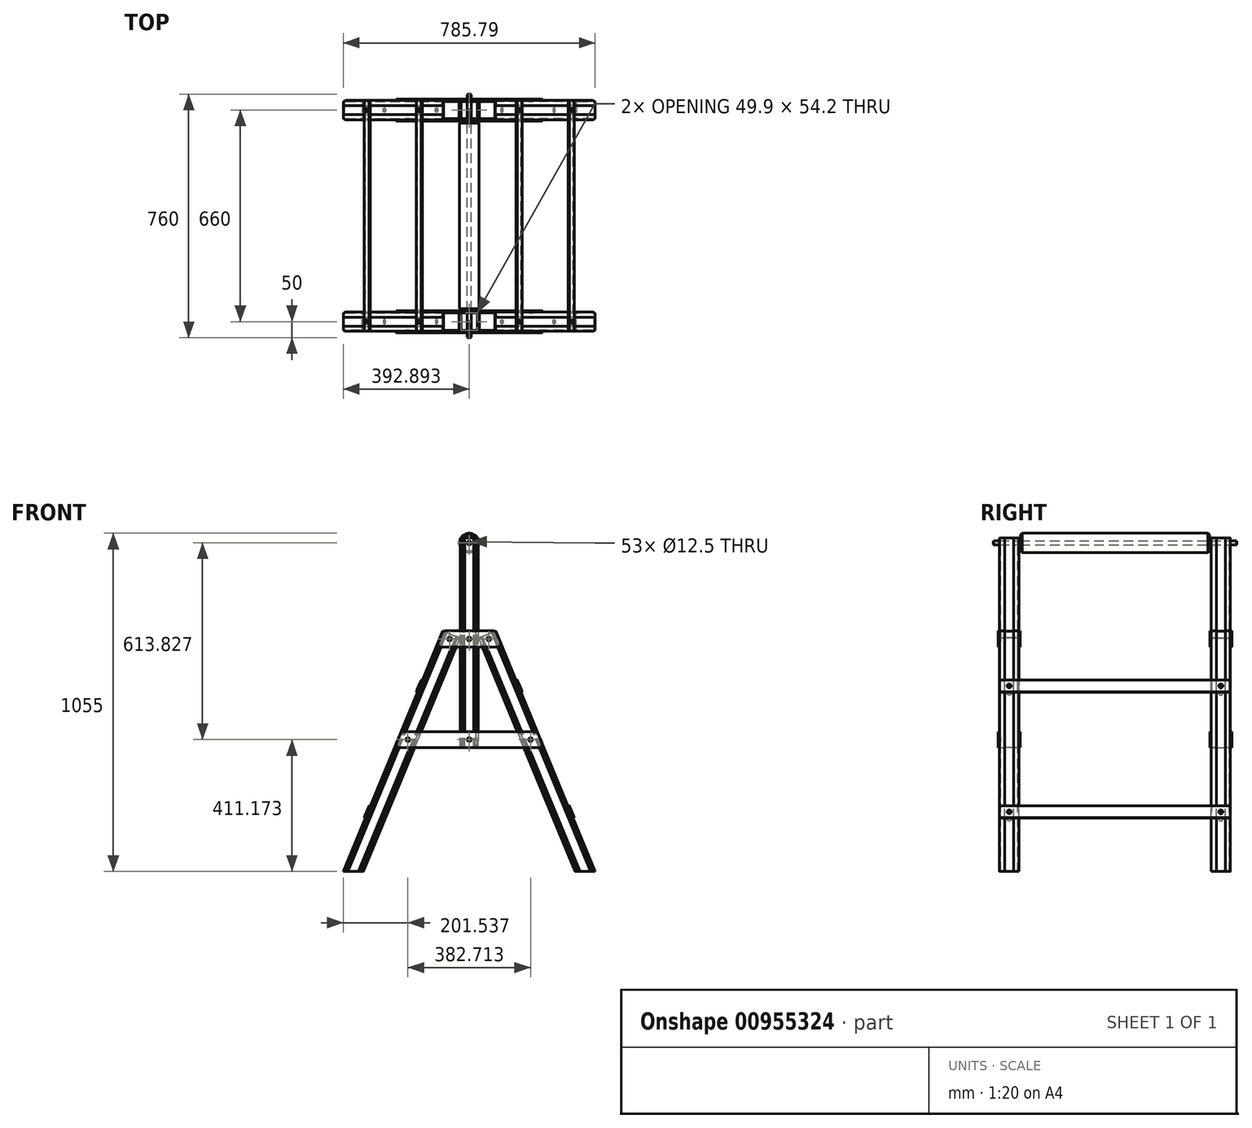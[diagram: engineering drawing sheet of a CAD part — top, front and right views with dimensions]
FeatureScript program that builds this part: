
annotation { "Feature Type Name" : "Feature", "Feature Type Description" : "" }
export const myFeature = defineFeature(function(context is Context, id is Id, definition is map)
    precondition{}
    {
        {
            var Q0;
            Q0=qCreatedBy(makeId("Front.planeOp"),FACE);
            var sketch = newSketch(context, id + "F0", { "sketchPlane" : qUnion([Q0])});
            skLineSegment(sketch, "E0", {"start": v(0, 0) * mm, "end": v(-310.74, 750.2) * mm});
            skLineSegment(sketch, "E1", {"start": v(-310.74, 750.2) * mm, "end": v(-364.05, 728.1) * mm});
            skLineSegment(sketch, "E2", {"start": v(-364.05, 728.1) * mm, "end": v(-62.45, 0) * mm});
            skLineSegment(sketch, "E3", {"start": v(-62.45, 0) * mm, "end": v(0, 0) * mm});
            skLineSegment(sketch, "E4", {"start": v(-337.4, 739.15) * mm, "end": v(-31.23, 0) * mm, "construction": true});
            skCircle(sketch, "E5", {"center": v(-331.65, 725.3) * mm, "radius": 6.25 * mm});
            skCircle(sketch, "E6", {"center": v(-201.54, 411.17) * mm, "radius": 6.25 * mm});
            skSolve(sketch);
        }
        {
            var Q0;
            Q0=qSketchRegion(id+"F0",true);
            extrude(context, id + "F1", {"entities" : qUnion([Q0]), "depth" : 60 * mm, "offsetDistance" : 25 * mm});
        }
        {
            var Q0;
            Q0=makeQuery(id+"F1.opExtrude","CAP_EDGE",EDGE,{"disambiguationData":[OSD([sQuery(id+"F0.wireOp",EDGE,"E0")])],"isStart":false});
            var Q1;
            Q1=makeQuery(id+"F1.opExtrude","CAP_EDGE",EDGE,{"disambiguationData":[OSD([sQuery(id+"F0.wireOp",EDGE,"E2")])],"isStart":false});
            var Q2;
            Q2=makeQuery(id+"F1.opExtrude","CAP_EDGE",EDGE,{"disambiguationData":[OSD([sQuery(id+"F0.wireOp",EDGE,"E0")])],"isStart":true});
            var Q3;
            Q3=makeQuery(id+"F1.opExtrude","CAP_EDGE",EDGE,{"disambiguationData":[OSD([sQuery(id+"F0.wireOp",EDGE,"E2")])],"isStart":true});
            fillet(context, id + "F2", {"entities" : qUnion([Q0, Q1, Q2, Q3]), "radius" : 7.5 * mm, "tangentPropagation" : true, "allowEdgeOverflow" : false});
        }
        {
            var Q0;
            Q0=makeQuery(id+"F1.opExtrude","SWEPT_FACE",FACE,{"disambiguationData":[OSD([sQuery(id+"F0.wireOp",EDGE,"E1")])]});
            var sketch = newSketch(context, id + "F3", { "sketchPlane" : qUnion([Q0])});
            skLineSegment(sketch, "E7", {"start": v(-50.2, -60) * mm, "end": v(-49.2, -59) * mm});
            skLineSegment(sketch, "E8", {"start": v(-49.2, -59) * mm, "end": v(-48.2, -60) * mm});
            skLineSegment(sketch, "E9", {"start": v(-48.2, -60) * mm, "end": v(-47.2, -59) * mm});
            skLineSegment(sketch, "E10", {"start": v(-47.2, -59) * mm, "end": v(-46.2, -60) * mm});
            skLineSegment(sketch, "E11", {"start": v(-46.2, -60) * mm, "end": v(-45.2, -59) * mm});
            skLineSegment(sketch, "E12", {"start": v(-45.2, -59) * mm, "end": v(-44.2, -60) * mm});
            skLineSegment(sketch, "E13", {"start": v(-28.85, -60) * mm, "end": v(-28.85, -30) * mm, "construction": true});
            skPoint(sketch, "E13.endSnap0", {"position": v(-57.7, -30) * mm});
            skLineSegment(sketch, "E14", {"start": v(-28.85, -30) * mm, "end": v(-57.7, -30) * mm, "construction": true});
            skLineSegment(sketch, "E15", {"start": v(-57.4, -44) * mm, "end": v(-57.7, -44) * mm});
            skLineSegment(sketch, "E16", {"start": v(-57.4, -44) * mm, "end": v(-57.4, -30) * mm});
            skArc(sketch, "E17.0", {"start": v(-54.8, -52.5) * mm, "mid": v(-53.45, -55.75) * mm, "end": v(-50.2, -57.1) * mm});
            skLineSegment(sketch, "E18", {"start": v(-54.8, -52.5) * mm, "end": v(-54.8, -30) * mm});
            skLineSegment(sketch, "E19", {"start": v(-50.2, -57.1) * mm, "end": v(-28.85, -57.1) * mm});
            skLineSegment(sketch, "E20.MirrorCS", {"start": v(-0.3, -44) * mm, "end": v(0, -44) * mm});
            skLineSegment(sketch, "E21.MirrorCS", {"start": v(-7.5, -60) * mm, "end": v(-8.5, -59) * mm});
            skLineSegment(sketch, "E22.MirrorCS", {"start": v(-11.5, -60) * mm, "end": v(-12.5, -59) * mm});
            skLineSegment(sketch, "E23.MirrorCS", {"start": v(-9.5, -60) * mm, "end": v(-10.5, -59) * mm});
            skLineSegment(sketch, "E24.MirrorCS", {"start": v(-12.5, -59) * mm, "end": v(-13.5, -60) * mm});
            skLineSegment(sketch, "E25.MirrorCS", {"start": v(-10.5, -59) * mm, "end": v(-11.5, -60) * mm});
            skLineSegment(sketch, "E26.MirrorCS", {"start": v(-8.5, -59) * mm, "end": v(-9.5, -60) * mm});
            skArc(sketch, "E27.MirrorCS", {"start": v(-2.9, -52.5) * mm, "mid": v(-4.25, -55.75) * mm, "end": v(-7.5, -57.1) * mm});
            skLineSegment(sketch, "E28.MirrorCS", {"start": v(-0.3, -44) * mm, "end": v(-0.3, -30) * mm});
            skLineSegment(sketch, "E29.MirrorCS", {"start": v(-7.5, -57.1) * mm, "end": v(-28.85, -57.1) * mm});
            skLineSegment(sketch, "E30.MirrorCS", {"start": v(-2.9, -52.5) * mm, "end": v(-2.9, -30) * mm});
            skLineSegment(sketch, "E31.MirrorCS", {"start": v(-50.2, 0) * mm, "end": v(-49.2, -1) * mm});
            skLineSegment(sketch, "E32.MirrorCS", {"start": v(-48.2, 0) * mm, "end": v(-47.2, -1) * mm});
            skLineSegment(sketch, "E33.MirrorCS", {"start": v(-49.2, -1) * mm, "end": v(-48.2, 0) * mm});
            skLineSegment(sketch, "E34.MirrorCS", {"start": v(-46.2, 0) * mm, "end": v(-45.2, -1) * mm});
            skLineSegment(sketch, "E35.MirrorCS", {"start": v(-47.2, -1) * mm, "end": v(-46.2, 0) * mm});
            skLineSegment(sketch, "E36.MirrorCS", {"start": v(-57.4, -16) * mm, "end": v(-57.7, -16) * mm});
            skLineSegment(sketch, "E37.MirrorCS", {"start": v(-45.2, -1) * mm, "end": v(-44.2, 0) * mm});
            skArc(sketch, "E38.MirrorCS", {"start": v(-54.8, -7.5) * mm, "mid": v(-53.45, -4.25) * mm, "end": v(-50.2, -2.9) * mm});
            skLineSegment(sketch, "E39.MirrorCS", {"start": v(-50.2, -2.9) * mm, "end": v(-28.85, -2.9) * mm});
            skLineSegment(sketch, "E40.MirrorCS", {"start": v(-54.8, -7.5) * mm, "end": v(-54.8, -30) * mm});
            skLineSegment(sketch, "E41.MirrorCS", {"start": v(-57.4, -16) * mm, "end": v(-57.4, -30) * mm});
            skLineSegment(sketch, "E42.MirrorCS", {"start": v(-9.5, 0) * mm, "end": v(-10.5, -1) * mm});
            skLineSegment(sketch, "E43.MirrorCS", {"start": v(-12.5, -1) * mm, "end": v(-13.5, 0) * mm});
            skLineSegment(sketch, "E44.MirrorCS", {"start": v(-10.5, -1) * mm, "end": v(-11.5, 0) * mm});
            skLineSegment(sketch, "E45.MirrorCS", {"start": v(-0.3, -16) * mm, "end": v(0, -16) * mm});
            skLineSegment(sketch, "E46.MirrorCS", {"start": v(-11.5, 0) * mm, "end": v(-12.5, -1) * mm});
            skLineSegment(sketch, "E47.MirrorCS", {"start": v(-7.5, 0) * mm, "end": v(-8.5, -1) * mm});
            skLineSegment(sketch, "E48.MirrorCS", {"start": v(-8.5, -1) * mm, "end": v(-9.5, 0) * mm});
            skLineSegment(sketch, "E49.MirrorCS", {"start": v(-2.9, -7.5) * mm, "end": v(-2.9, -30) * mm});
            skLineSegment(sketch, "E50.MirrorCS", {"start": v(-7.5, -2.9) * mm, "end": v(-28.85, -2.9) * mm});
            skArc(sketch, "E51.MirrorCS", {"start": v(-2.9, -7.5) * mm, "mid": v(-4.25, -4.25) * mm, "end": v(-7.5, -2.9) * mm});
            skLineSegment(sketch, "E52.MirrorCS", {"start": v(-0.3, -16) * mm, "end": v(-0.3, -30) * mm});
            skSolve(sketch);
        }
        {
            var Q0;
            Q0=makeQuery(id+"F3.imprint","IMPRINT",FACE,{"disambiguationData":[TD([[makeQuery(id+"F3.imprint","IMPRINT",EDGE,{"derivedFrom":sQuery(id+"F3.wireOp",EDGE,"E17.0")}),1.0]])]});
            var Q1;
            {var subQ0=sQuery(id+"F3.wireOp",EDGE,"E34.MirrorCS");Q1=makeQuery(id+"F3.imprint","IMPRINT",FACE,{"disambiguationData":[TD([[makeQuery(id+"F3.imprint","IMPRINT",EDGE,{"derivedFrom":subQ0}),1.0]])]});}
            var Q2;
            {var subQ0=sQuery(id+"F3.wireOp",EDGE,"E32.MirrorCS");Q2=makeQuery(id+"F3.imprint","IMPRINT",FACE,{"disambiguationData":[TD([[makeQuery(id+"F3.imprint","IMPRINT",EDGE,{"derivedFrom":subQ0}),1.0]])]});}
            var Q3;
            {var subQ0=sQuery(id+"F3.wireOp",EDGE,"E31.MirrorCS");Q3=makeQuery(id+"F3.imprint","IMPRINT",FACE,{"disambiguationData":[TD([[makeQuery(id+"F3.imprint","IMPRINT",EDGE,{"derivedFrom":subQ0}),1.0]])]});}
            var Q4;
            {var subQ1=sQuery(id+"F3.wireOp",EDGE,"E15");Q4=makeQuery(id+"F3.imprint","IMPRINT",FACE,{"disambiguationData":[TD([[makeQuery(id+"F3.imprint","IMPRINT",EDGE,{"derivedFrom":subQ1}),-1.0]])]});}
            var Q5;
            {var subQ0=sQuery(id+"F3.wireOp",EDGE,"E7");Q5=makeQuery(id+"F3.imprint","IMPRINT",FACE,{"disambiguationData":[TD([[makeQuery(id+"F3.imprint","IMPRINT",EDGE,{"derivedFrom":subQ0}),-1.0]])]});}
            var Q6;
            {var subQ0=sQuery(id+"F3.wireOp",EDGE,"E9");Q6=makeQuery(id+"F3.imprint","IMPRINT",FACE,{"disambiguationData":[TD([[makeQuery(id+"F3.imprint","IMPRINT",EDGE,{"derivedFrom":subQ0}),-1.0]])]});}
            var Q7;
            {var subQ0=sQuery(id+"F3.wireOp",EDGE,"E11");Q7=makeQuery(id+"F3.imprint","IMPRINT",FACE,{"disambiguationData":[TD([[makeQuery(id+"F3.imprint","IMPRINT",EDGE,{"derivedFrom":subQ0}),-1.0]])]});}
            var Q8;
            {var subQ0=sQuery(id+"F3.wireOp",EDGE,"E21.MirrorCS");Q8=makeQuery(id+"F3.imprint","IMPRINT",FACE,{"disambiguationData":[TD([[makeQuery(id+"F3.imprint","IMPRINT",EDGE,{"derivedFrom":subQ0}),1.0]])]});}
            var Q9;
            {var subQ0=sQuery(id+"F3.wireOp",EDGE,"E23.MirrorCS");Q9=makeQuery(id+"F3.imprint","IMPRINT",FACE,{"disambiguationData":[TD([[makeQuery(id+"F3.imprint","IMPRINT",EDGE,{"derivedFrom":subQ0}),1.0]])]});}
            var Q10;
            {var subQ0=sQuery(id+"F3.wireOp",EDGE,"E22.MirrorCS");Q10=makeQuery(id+"F3.imprint","IMPRINT",FACE,{"disambiguationData":[TD([[makeQuery(id+"F3.imprint","IMPRINT",EDGE,{"derivedFrom":subQ0}),1.0]])]});}
            var Q11;
            {var subQ1=sQuery(id+"F3.wireOp",EDGE,"E20.MirrorCS");Q11=makeQuery(id+"F3.imprint","IMPRINT",FACE,{"disambiguationData":[TD([[makeQuery(id+"F3.imprint","IMPRINT",EDGE,{"derivedFrom":subQ1}),1.0]])]});}
            var Q12;
            {var subQ0=sQuery(id+"F3.wireOp",EDGE,"E47.MirrorCS");Q12=makeQuery(id+"F3.imprint","IMPRINT",FACE,{"disambiguationData":[TD([[makeQuery(id+"F3.imprint","IMPRINT",EDGE,{"derivedFrom":subQ0}),-1.0]])]});}
            var Q13;
            {var subQ0=sQuery(id+"F3.wireOp",EDGE,"E42.MirrorCS");Q13=makeQuery(id+"F3.imprint","IMPRINT",FACE,{"disambiguationData":[TD([[makeQuery(id+"F3.imprint","IMPRINT",EDGE,{"derivedFrom":subQ0}),-1.0]])]});}
            var Q14;
            {var subQ0=sQuery(id+"F3.wireOp",EDGE,"E43.MirrorCS");Q14=makeQuery(id+"F3.imprint","IMPRINT",FACE,{"disambiguationData":[TD([[makeQuery(id+"F3.imprint","IMPRINT",EDGE,{"derivedFrom":subQ0}),-1.0]])]});}
            var Q15;
            Q15=makeQuery(id+"F1.opExtrude","SWEPT_FACE",FACE,{"disambiguationData":[OSD([sQuery(id+"F0.wireOp",EDGE,"E3")])]});
            extrude(context, id + "F4", {"entities" : qUnion([Q0, Q1, Q2, Q3, Q4, Q5, Q6, Q7, Q8, Q9, Q10, Q11, Q12, Q13, Q14]), "operationType" : NewBodyOperationType.REMOVE, "endBound" : BoundingType.UP_TO_SURFACE, "oppositeDirection" : true, "depth" : 25 * mm, "endBoundEntityFace" : qUnion([Q15]), "offsetDistance" : 25 * mm});
        }
        {
            var Q0;
            {var subQ0=sQuery(id+"F0.wireOp",EDGE,"E0");Q0=makeQuery(id+"F4.boolean.opBoolean","SPLIT",FACE,{"disambiguationData":[TD([makeQuery(id+"F4.opExtrude","SWEPT_FACE",FACE,{"disambiguationData":[OSD([sQuery(id+"F3.wireOp",EDGE,"E20.MirrorCS")])]})])],"derivedFrom":makeQuery(id+"F1.opExtrude","SWEPT_FACE",FACE,{"disambiguationData":[OSD([subQ0])]})});}
            var sketch = newSketch(context, id + "F5", { "sketchPlane" : qUnion([Q0])});
            skLineSegment(sketch, "E53", {"start": v(-60, 0) * mm, "end": v(0, 0) * mm, "construction": true});
            skLineSegment(sketch, "E54", {"start": v(-30, 0) * mm, "end": v(-30, 812) * mm, "construction": true});
            skCircle(sketch, "E55", {"center": v(-30, 200) * mm, "radius": 6.25 * mm});
            skCircle(sketch, "E56", {"center": v(-30, 625) * mm, "radius": 6.25 * mm});
            skSolve(sketch);
        }
        {
            var Q0;
            Q0=qSketchRegion(id+"F5",true);
            var Q1;
            {var subQ0=sQuery(id+"F0.wireOp",EDGE,"E2");Q1=makeQuery(id+"F4.boolean.opBoolean","SPLIT",FACE,{"disambiguationData":[TD([makeQuery(id+"F4.opExtrude","SWEPT_FACE",FACE,{"disambiguationData":[OSD([sQuery(id+"F3.wireOp",EDGE,"E15")])]})])],"derivedFrom":makeQuery(id+"F1.opExtrude","SWEPT_FACE",FACE,{"disambiguationData":[OSD([subQ0])]})});}
            extrude(context, id + "F6", {"entities" : qUnion([Q0]), "operationType" : NewBodyOperationType.REMOVE, "endBound" : BoundingType.UP_TO_SURFACE, "oppositeDirection" : true, "depth" : 25 * mm, "endBoundEntityFace" : qUnion([Q1]), "offsetDistance" : 25 * mm});
        }
        {
            var Q0;
            Q0=makeQuery(id+"F1.opExtrude","CAP_FACE",FACE,{"disambiguationData":[OSD([sQuery(id+"F0.wireOp",EDGE,"E0"),sQuery(id+"F0.wireOp",EDGE,"E1"),sQuery(id+"F0.wireOp",EDGE,"E2"),sQuery(id+"F0.wireOp",EDGE,"E3")])],"isStart":false});
            var sketch = newSketch(context, id + "F7", { "sketchPlane" : qUnion([Q0])});
            skLineSegment(sketch, "E57", {"start": v(-365.05, 1040) * mm, "end": v(-365.05, 386.17) * mm});
            skLineSegment(sketch, "E58", {"start": v(-365.05, 386.17) * mm, "end": v(-420.75, 386.17) * mm});
            skLineSegment(sketch, "E59", {"start": v(-420.75, 386.17) * mm, "end": v(-420.75, 1040) * mm});
            skLineSegment(sketch, "E60", {"start": v(-420.75, 1040) * mm, "end": v(-365.05, 1040) * mm});
            skLineSegment(sketch, "E61", {"start": v(-392.9, 386.17) * mm, "end": v(-392.9, 1040) * mm, "construction": true});
            skCircle(sketch, "E62", {"center": v(-392.9, 725.3) * mm, "radius": 6.25 * mm});
            skLineSegment(sketch, "E63", {"start": v(-420.75, 719.04) * mm, "end": v(-297.84, 719.04) * mm, "construction": true});
            skLineSegment(sketch, "E64", {"start": v(-420.75, 404.92) * mm, "end": v(-167.72, 404.92) * mm, "construction": true});
            skCircle(sketch, "E65", {"center": v(-392.9, 411.17) * mm, "radius": 6.25 * mm});
            skCircle(sketch, "E66", {"center": v(-392.9, 1025) * mm, "radius": 6.25 * mm});
            skSolve(sketch);
        }
        {
            var Q0;
            Q0=qSketchRegion(id+"F7",true);
            extrude(context, id + "F8", {"entities" : qUnion([Q0]), "oppositeDirection" : true, "depth" : 60 * mm, "offsetDistance" : 25 * mm});
        }
        {
            var Q0;
            Q0=makeQuery(id+"F8.opExtrude","CAP_EDGE",EDGE,{"disambiguationData":[OSD([sQuery(id+"F7.wireOp",EDGE,"E59")])],"isStart":true});
            var Q1;
            Q1=makeQuery(id+"F8.opExtrude","CAP_EDGE",EDGE,{"disambiguationData":[OSD([sQuery(id+"F7.wireOp",EDGE,"E57")])],"isStart":true});
            var Q2;
            Q2=makeQuery(id+"F8.opExtrude","CAP_EDGE",EDGE,{"disambiguationData":[OSD([sQuery(id+"F7.wireOp",EDGE,"E57")])],"isStart":false});
            var Q3;
            Q3=makeQuery(id+"F8.opExtrude","CAP_EDGE",EDGE,{"disambiguationData":[OSD([sQuery(id+"F7.wireOp",EDGE,"E59")])],"isStart":false});
            fillet(context, id + "F9", {"entities" : qUnion([Q0, Q1, Q2, Q3]), "radius" : 7.5 * mm, "tangentPropagation" : true, "allowEdgeOverflow" : false});
        }
        {
            var Q0;
            Q0=makeQuery(id+"F8.opExtrude","SWEPT_FACE",FACE,{"disambiguationData":[OSD([sQuery(id+"F7.wireOp",EDGE,"E60")])]});
            var sketch = newSketch(context, id + "F10", { "sketchPlane" : qUnion([Q0])});
            skLineSegment(sketch, "E67", {"start": v(-420.75, -30) * mm, "end": v(-392.9, -30) * mm, "construction": true});
            skPoint(sketch, "E67.endSnap0", {"position": v(-392.9, -60) * mm});
            skLineSegment(sketch, "E68", {"start": v(-392.9, -30) * mm, "end": v(-392.9, -60) * mm, "construction": true});
            skLineSegment(sketch, "E69", {"start": v(-413.25, -60) * mm, "end": v(-412.25, -59) * mm});
            skLineSegment(sketch, "E70", {"start": v(-412.25, -59) * mm, "end": v(-411.25, -60) * mm});
            skLineSegment(sketch, "E71", {"start": v(-420.45, -30) * mm, "end": v(-420.45, -44) * mm});
            skLineSegment(sketch, "E72", {"start": v(-420.45, -44) * mm, "end": v(-420.75, -44) * mm});
            skLineSegment(sketch, "E73", {"start": v(-411.25, -60) * mm, "end": v(-410.25, -59) * mm});
            skLineSegment(sketch, "E74", {"start": v(-410.25, -59) * mm, "end": v(-409.25, -60) * mm});
            skLineSegment(sketch, "E75", {"start": v(-409.25, -60) * mm, "end": v(-408.25, -59) * mm});
            skLineSegment(sketch, "E76", {"start": v(-408.25, -59) * mm, "end": v(-407.25, -60) * mm});
            skArc(sketch, "E77.0", {"start": v(-417.85, -52.5) * mm, "mid": v(-416.5, -55.75) * mm, "end": v(-413.25, -57.1) * mm});
            skLineSegment(sketch, "E78", {"start": v(-417.85, -52.5) * mm, "end": v(-417.85, -30) * mm});
            skLineSegment(sketch, "E79", {"start": v(-413.25, -57.1) * mm, "end": v(-392.9, -57.1) * mm});
            skLineSegment(sketch, "E80.MirrorCS", {"start": v(-365.35, -44) * mm, "end": v(-365.05, -44) * mm});
            skLineSegment(sketch, "E81.MirrorCS", {"start": v(-372.55, -60) * mm, "end": v(-373.55, -59) * mm});
            skLineSegment(sketch, "E82.MirrorCS", {"start": v(-373.55, -59) * mm, "end": v(-374.55, -60) * mm});
            skLineSegment(sketch, "E83.MirrorCS", {"start": v(-377.55, -59) * mm, "end": v(-378.55, -60) * mm});
            skLineSegment(sketch, "E84.MirrorCS", {"start": v(-374.55, -60) * mm, "end": v(-375.55, -59) * mm});
            skLineSegment(sketch, "E85.MirrorCS", {"start": v(-375.55, -59) * mm, "end": v(-376.55, -60) * mm});
            skLineSegment(sketch, "E86.MirrorCS", {"start": v(-376.55, -60) * mm, "end": v(-377.55, -59) * mm});
            skArc(sketch, "E87.MirrorCS", {"start": v(-367.95, -52.5) * mm, "mid": v(-369.3, -55.75) * mm, "end": v(-372.55, -57.1) * mm});
            skLineSegment(sketch, "E88.MirrorCS", {"start": v(-365.35, -30) * mm, "end": v(-365.35, -44) * mm});
            skLineSegment(sketch, "E89.MirrorCS", {"start": v(-372.55, -57.1) * mm, "end": v(-392.9, -57.1) * mm});
            skLineSegment(sketch, "E90.MirrorCS", {"start": v(-367.95, -52.5) * mm, "end": v(-367.95, -30) * mm});
            skLineSegment(sketch, "E91.MirrorCS", {"start": v(-411.25, 0) * mm, "end": v(-410.25, -1) * mm});
            skLineSegment(sketch, "E92.MirrorCS", {"start": v(-413.25, 0) * mm, "end": v(-412.25, -1) * mm});
            skLineSegment(sketch, "E93.MirrorCS", {"start": v(-412.25, -1) * mm, "end": v(-411.25, 0) * mm});
            skLineSegment(sketch, "E94.MirrorCS", {"start": v(-410.25, -1) * mm, "end": v(-409.25, 0) * mm});
            skLineSegment(sketch, "E95.MirrorCS", {"start": v(-420.45, -16) * mm, "end": v(-420.75, -16) * mm});
            skLineSegment(sketch, "E96.MirrorCS", {"start": v(-409.25, 0) * mm, "end": v(-408.25, -1) * mm});
            skLineSegment(sketch, "E97.MirrorCS", {"start": v(-408.25, -1) * mm, "end": v(-407.25, 0) * mm});
            skArc(sketch, "E98.MirrorCS", {"start": v(-417.85, -7.5) * mm, "mid": v(-416.5, -4.25) * mm, "end": v(-413.25, -2.9) * mm});
            skLineSegment(sketch, "E99.MirrorCS", {"start": v(-413.25, -2.9) * mm, "end": v(-392.9, -2.9) * mm});
            skLineSegment(sketch, "E100.MirrorCS", {"start": v(-417.85, -7.5) * mm, "end": v(-417.85, -30) * mm});
            skLineSegment(sketch, "E101.MirrorCS", {"start": v(-420.45, -30) * mm, "end": v(-420.45, -16) * mm});
            skLineSegment(sketch, "E102.MirrorCS", {"start": v(-375.55, -1) * mm, "end": v(-376.55, 0) * mm});
            skLineSegment(sketch, "E103.MirrorCS", {"start": v(-376.55, 0) * mm, "end": v(-377.55, -1) * mm});
            skLineSegment(sketch, "E104.MirrorCS", {"start": v(-372.55, 0) * mm, "end": v(-373.55, -1) * mm});
            skLineSegment(sketch, "E105.MirrorCS", {"start": v(-373.55, -1) * mm, "end": v(-374.55, 0) * mm});
            skLineSegment(sketch, "E106.MirrorCS", {"start": v(-374.55, 0) * mm, "end": v(-375.55, -1) * mm});
            skLineSegment(sketch, "E107.MirrorCS", {"start": v(-365.35, -16) * mm, "end": v(-365.05, -16) * mm});
            skLineSegment(sketch, "E108.MirrorCS", {"start": v(-377.55, -1) * mm, "end": v(-378.55, 0) * mm});
            skArc(sketch, "E109.MirrorCS", {"start": v(-367.95, -7.5) * mm, "mid": v(-369.3, -4.25) * mm, "end": v(-372.55, -2.9) * mm});
            skLineSegment(sketch, "E110.MirrorCS", {"start": v(-365.35, -30) * mm, "end": v(-365.35, -16) * mm});
            skLineSegment(sketch, "E111.MirrorCS", {"start": v(-367.95, -7.5) * mm, "end": v(-367.95, -30) * mm});
            skLineSegment(sketch, "E112.MirrorCS", {"start": v(-372.55, -2.9) * mm, "end": v(-392.9, -2.9) * mm});
            skSolve(sketch);
        }
        {
            var Q0;
            {var subQ0=sQuery(id+"F10.wireOp",EDGE,"E69");Q0=makeQuery(id+"F10.imprint","IMPRINT",FACE,{"disambiguationData":[TD([[makeQuery(id+"F10.imprint","IMPRINT",EDGE,{"derivedFrom":subQ0}),-1.0]])]});}
            var Q1;
            {var subQ0=sQuery(id+"F10.wireOp",EDGE,"E73");Q1=makeQuery(id+"F10.imprint","IMPRINT",FACE,{"disambiguationData":[TD([[makeQuery(id+"F10.imprint","IMPRINT",EDGE,{"derivedFrom":subQ0}),-1.0]])]});}
            var Q2;
            {var subQ0=sQuery(id+"F10.wireOp",EDGE,"E75");Q2=makeQuery(id+"F10.imprint","IMPRINT",FACE,{"disambiguationData":[TD([[makeQuery(id+"F10.imprint","IMPRINT",EDGE,{"derivedFrom":subQ0}),-1.0]])]});}
            var Q3;
            {var subQ0=sQuery(id+"F10.wireOp",EDGE,"E83.MirrorCS");Q3=makeQuery(id+"F10.imprint","IMPRINT",FACE,{"disambiguationData":[TD([[makeQuery(id+"F10.imprint","IMPRINT",EDGE,{"derivedFrom":subQ0}),1.0]])]});}
            var Q4;
            {var subQ0=sQuery(id+"F10.wireOp",EDGE,"E84.MirrorCS");Q4=makeQuery(id+"F10.imprint","IMPRINT",FACE,{"disambiguationData":[TD([[makeQuery(id+"F10.imprint","IMPRINT",EDGE,{"derivedFrom":subQ0}),1.0]])]});}
            var Q5;
            {var subQ0=sQuery(id+"F10.wireOp",EDGE,"E81.MirrorCS");Q5=makeQuery(id+"F10.imprint","IMPRINT",FACE,{"disambiguationData":[TD([[makeQuery(id+"F10.imprint","IMPRINT",EDGE,{"derivedFrom":subQ0}),1.0]])]});}
            var Q6;
            Q6=makeQuery(id+"F10.imprint","IMPRINT",FACE,{"disambiguationData":[TD([[makeQuery(id+"F10.imprint","IMPRINT",EDGE,{"derivedFrom":sQuery(id+"F10.wireOp",EDGE,"E71")}),-1.0]])]});
            var Q7;
            {var subQ1=sQuery(id+"F10.wireOp",EDGE,"E80.MirrorCS");Q7=makeQuery(id+"F10.imprint","IMPRINT",FACE,{"disambiguationData":[TD([[makeQuery(id+"F10.imprint","IMPRINT",EDGE,{"derivedFrom":subQ1}),1.0]])]});}
            var Q8;
            {var subQ0=sQuery(id+"F10.wireOp",EDGE,"E103.MirrorCS");Q8=makeQuery(id+"F10.imprint","IMPRINT",FACE,{"disambiguationData":[TD([[makeQuery(id+"F10.imprint","IMPRINT",EDGE,{"derivedFrom":subQ0}),-1.0]])]});}
            var Q9;
            {var subQ0=sQuery(id+"F10.wireOp",EDGE,"E102.MirrorCS");Q9=makeQuery(id+"F10.imprint","IMPRINT",FACE,{"disambiguationData":[TD([[makeQuery(id+"F10.imprint","IMPRINT",EDGE,{"derivedFrom":subQ0}),-1.0]])]});}
            var Q10;
            {var subQ0=sQuery(id+"F10.wireOp",EDGE,"E104.MirrorCS");Q10=makeQuery(id+"F10.imprint","IMPRINT",FACE,{"disambiguationData":[TD([[makeQuery(id+"F10.imprint","IMPRINT",EDGE,{"derivedFrom":subQ0}),-1.0]])]});}
            var Q11;
            {var subQ0=sQuery(id+"F10.wireOp",EDGE,"E92.MirrorCS");Q11=makeQuery(id+"F10.imprint","IMPRINT",FACE,{"disambiguationData":[TD([[makeQuery(id+"F10.imprint","IMPRINT",EDGE,{"derivedFrom":subQ0}),1.0]])]});}
            var Q12;
            {var subQ0=sQuery(id+"F10.wireOp",EDGE,"E91.MirrorCS");Q12=makeQuery(id+"F10.imprint","IMPRINT",FACE,{"disambiguationData":[TD([[makeQuery(id+"F10.imprint","IMPRINT",EDGE,{"derivedFrom":subQ0}),1.0]])]});}
            var Q13;
            {var subQ0=sQuery(id+"F10.wireOp",EDGE,"E96.MirrorCS");Q13=makeQuery(id+"F10.imprint","IMPRINT",FACE,{"disambiguationData":[TD([[makeQuery(id+"F10.imprint","IMPRINT",EDGE,{"derivedFrom":subQ0}),1.0]])]});}
            var Q14;
            Q14=makeQuery(id+"F10.imprint","IMPRINT",FACE,{"disambiguationData":[TD([[makeQuery(id+"F10.imprint","IMPRINT",EDGE,{"derivedFrom":sQuery(id+"F10.wireOp",EDGE,"E77.0")}),1.0]])]});
            var Q15;
            Q15=makeQuery(id+"F8.opExtrude","SWEPT_FACE",FACE,{"disambiguationData":[OSD([sQuery(id+"F7.wireOp",EDGE,"E58")])]});
            extrude(context, id + "F11", {"entities" : qUnion([Q0, Q1, Q2, Q3, Q4, Q5, Q6, Q7, Q8, Q9, Q10, Q11, Q12, Q13, Q14]), "operationType" : NewBodyOperationType.REMOVE, "endBound" : BoundingType.UP_TO_SURFACE, "oppositeDirection" : true, "depth" : 25 * mm, "endBoundEntityFace" : qUnion([Q15]), "offsetDistance" : 25 * mm});
        }
        {
            var Q0;
            Q0=makeQuery(id+"F11.boolean.opBoolean","COPY",FACE,{"derivedFrom":makeQuery(id+"F11.opExtrude","SWEPT_FACE",FACE,{"disambiguationData":[OSD([sQuery(id+"F10.wireOp",EDGE,"E88.MirrorCS"),sQuery(id+"F10.wireOp",EDGE,"E110.MirrorCS")])]})});
            var Q1;
            Q1=makeQuery(id+"F11.boolean.opBoolean","COPY",FACE,{"derivedFrom":makeQuery(id+"F11.opExtrude","SWEPT_FACE",FACE,{"disambiguationData":[OSD([sQuery(id+"F10.wireOp",EDGE,"E71"),sQuery(id+"F10.wireOp",EDGE,"E101.MirrorCS")])]})});
            cPlane(context, id + "F12", {"entities" : qUnion([Q0, Q1]), "cplaneType" : CPlaneType.MID_PLANE, "offset" : 25 * mm, "width" : 150 * mm, "height" : 150 * mm});
        }
        {
            var Q0;
            Q0=makeQuery(id+"F1.opExtrude","SWEPT_BODY",BODY,{"disambiguationData":[OSD([sQuery(id+"F0.wireOp",EDGE,"E0"),sQuery(id+"F0.wireOp",EDGE,"E1"),sQuery(id+"F0.wireOp",EDGE,"E2"),sQuery(id+"F0.wireOp",EDGE,"E3")])]});
            var Q1;
            Q1=qCreatedBy(id+"F12.planeOp",FACE);
            mirror(context, id + "F13", {"entities" : qUnion([Q0]), "mirrorPlane" : qUnion([Q1])});
        }
        {
            var Q0;
            Q0=makeQuery(id+"F13.opPattern","COPY",FACE,{"derivedFrom":makeQuery(id+"F1.opExtrude","CAP_FACE",FACE,{"disambiguationData":[OSD([sQuery(id+"F0.wireOp",EDGE,"E0"),sQuery(id+"F0.wireOp",EDGE,"E1"),sQuery(id+"F0.wireOp",EDGE,"E2"),sQuery(id+"F0.wireOp",EDGE,"E3")])],"isStart":false}),"instanceName":"1"});
            var sketch = newSketch(context, id + "F14", { "sketchPlane" : qUnion([Q0])});
            skLineSegment(sketch, "E113", {"start": v(-605.13, 436.17) * mm, "end": v(-625.84, 386.17) * mm});
            skLineSegment(sketch, "E114", {"start": v(-625.84, 386.17) * mm, "end": v(-159.96, 386.17) * mm});
            skLineSegment(sketch, "E115", {"start": v(-159.96, 386.17) * mm, "end": v(-180.67, 436.17) * mm});
            skLineSegment(sketch, "E116", {"start": v(-180.67, 436.17) * mm, "end": v(-605.13, 436.17) * mm});
            skLineSegment(sketch, "E117", {"start": v(-475.05, 750.2) * mm, "end": v(-495.77, 700.2) * mm});
            skLineSegment(sketch, "E118", {"start": v(-495.77, 700.2) * mm, "end": v(-290.03, 700.2) * mm});
            skLineSegment(sketch, "E119", {"start": v(-290.03, 700.2) * mm, "end": v(-310.74, 750.2) * mm});
            skLineSegment(sketch, "E120", {"start": v(-310.74, 750.2) * mm, "end": v(-475.05, 750.2) * mm});
            skLineSegment(sketch, "E121", {"start": v(-392.9, 750.2) * mm, "end": v(-392.9, 700.2) * mm, "construction": true});
            skLineSegment(sketch, "E122", {"start": v(-485.4, 725.2) * mm, "end": v(-300.38, 725.2) * mm, "construction": true});
            skLineSegment(sketch, "E123", {"start": v(-615.48, 411.17) * mm, "end": v(-170.31, 411.17) * mm, "construction": true});
            skLineSegment(sketch, "E124", {"start": v(-392.9, 436.17) * mm, "end": v(-392.9, 386.17) * mm, "construction": true});
            skCircle(sketch, "E125", {"center": v(-392.9, 411.17) * mm, "radius": 6.25 * mm});
            skCircle(sketch, "E126", {"center": v(-392.9, 725.2) * mm, "radius": 6.25 * mm});
            skCircle(sketch, "E127", {"center": v(-454.14, 725.3) * mm, "radius": 6.25 * mm});
            skCircle(sketch, "E128", {"center": v(-331.65, 725.3) * mm, "radius": 6.25 * mm});
            skCircle(sketch, "E129", {"center": v(-201.54, 411.17) * mm, "radius": 6.25 * mm});
            skCircle(sketch, "E130", {"center": v(-584.25, 411.17) * mm, "radius": 6.25 * mm});
            skSolve(sketch);
        }
        {
            var Q0;
            Q0=qSketchRegion(id+"F14",true);
            extrude(context, id + "F15", {"entities" : qUnion([Q0]), "depth" : 4 * mm, "offsetDistance" : 25 * mm});
        }
        {
            var Q0;
            Q0=makeQuery(id+"F15.opExtrude","SWEPT_EDGE",EDGE,{"disambiguationData":[OSD([sQuery(id+"F14.wireOp",EDGE,"E117"),sQuery(id+"F14.wireOp",EDGE,"E120")])]});
            var Q1;
            Q1=makeQuery(id+"F15.opExtrude","SWEPT_EDGE",EDGE,{"disambiguationData":[OSD([sQuery(id+"F14.wireOp",EDGE,"E117"),sQuery(id+"F14.wireOp",EDGE,"E118")])]});
            var Q2;
            Q2=makeQuery(id+"F15.opExtrude","SWEPT_EDGE",EDGE,{"disambiguationData":[OSD([sQuery(id+"F14.wireOp",EDGE,"E119"),sQuery(id+"F14.wireOp",EDGE,"E120")])]});
            var Q3;
            Q3=makeQuery(id+"F15.opExtrude","SWEPT_EDGE",EDGE,{"disambiguationData":[OSD([sQuery(id+"F14.wireOp",EDGE,"E118"),sQuery(id+"F14.wireOp",EDGE,"E119")])]});
            var Q4;
            Q4=makeQuery(id+"F15.opExtrude","SWEPT_EDGE",EDGE,{"disambiguationData":[OSD([sQuery(id+"F14.wireOp",EDGE,"E113"),sQuery(id+"F14.wireOp",EDGE,"E114")])]});
            var Q5;
            Q5=makeQuery(id+"F15.opExtrude","SWEPT_EDGE",EDGE,{"disambiguationData":[OSD([sQuery(id+"F14.wireOp",EDGE,"E113"),sQuery(id+"F14.wireOp",EDGE,"E116")])]});
            var Q6;
            Q6=makeQuery(id+"F15.opExtrude","SWEPT_EDGE",EDGE,{"disambiguationData":[OSD([sQuery(id+"F14.wireOp",EDGE,"E115"),sQuery(id+"F14.wireOp",EDGE,"E116")])]});
            var Q7;
            Q7=makeQuery(id+"F15.opExtrude","SWEPT_EDGE",EDGE,{"disambiguationData":[OSD([sQuery(id+"F14.wireOp",EDGE,"E114"),sQuery(id+"F14.wireOp",EDGE,"E115")])]});
            fillet(context, id + "F16", {"entities" : qUnion([Q0, Q1, Q2, Q3, Q4, Q5, Q6, Q7]), "radius" : 10 * mm, "tangentPropagation" : true, "allowEdgeOverflow" : false});
        }
        {
            var Q0;
            Q0=makeQuery(id+"F11.boolean.opBoolean","COPY",FACE,{"derivedFrom":makeQuery(id+"F11.opExtrude","SWEPT_FACE",FACE,{"disambiguationData":[OSD([sQuery(id+"F10.wireOp",EDGE,"E99.MirrorCS"),sQuery(id+"F10.wireOp",EDGE,"E112.MirrorCS")])]})});
            var Q1;
            Q1=makeQuery(id+"F11.boolean.opBoolean","COPY",FACE,{"derivedFrom":makeQuery(id+"F11.opExtrude","SWEPT_FACE",FACE,{"disambiguationData":[OSD([sQuery(id+"F10.wireOp",EDGE,"E79"),sQuery(id+"F10.wireOp",EDGE,"E89.MirrorCS")])]})});
            cPlane(context, id + "F17", {"entities" : qUnion([Q0, Q1]), "cplaneType" : CPlaneType.MID_PLANE, "offset" : 25 * mm, "width" : 150 * mm, "height" : 150 * mm});
        }
        {
            var Q0;
            Q0=makeQuery(id+"F15.opExtrude","SWEPT_BODY",BODY,{"disambiguationData":[OSD([sQuery(id+"F14.wireOp",EDGE,"E113"),sQuery(id+"F14.wireOp",EDGE,"E114"),sQuery(id+"F14.wireOp",EDGE,"E115"),sQuery(id+"F14.wireOp",EDGE,"E116"),sQuery(id+"F14.wireOp",EDGE,"E125"),sQuery(id+"F14.wireOp",EDGE,"E129"),sQuery(id+"F14.wireOp",EDGE,"E130")])]});
            var Q1;
            Q1=makeQuery(id+"F15.opExtrude","SWEPT_BODY",BODY,{"disambiguationData":[OSD([sQuery(id+"F14.wireOp",EDGE,"E117"),sQuery(id+"F14.wireOp",EDGE,"E118"),sQuery(id+"F14.wireOp",EDGE,"E119"),sQuery(id+"F14.wireOp",EDGE,"E120"),sQuery(id+"F14.wireOp",EDGE,"E126"),sQuery(id+"F14.wireOp",EDGE,"E127"),sQuery(id+"F14.wireOp",EDGE,"E128")])]});
            var Q2;
            Q2=qCreatedBy(id+"F17.planeOp",FACE);
            mirror(context, id + "F18", {"entities" : qUnion([Q0, Q1]), "mirrorPlane" : qUnion([Q2])});
        }
        {
            var Q0;
            Q0=makeQuery(id+"F8.opExtrude","CAP_FACE",FACE,{"disambiguationData":[OSD([sQuery(id+"F7.wireOp",EDGE,"E57"),sQuery(id+"F7.wireOp",EDGE,"E58"),sQuery(id+"F7.wireOp",EDGE,"E59"),sQuery(id+"F7.wireOp",EDGE,"E60"),sQuery(id+"F7.wireOp",EDGE,"E62"),sQuery(id+"F7.wireOp",EDGE,"E65"),sQuery(id+"F7.wireOp",EDGE,"E66")])],"isStart":true});
            cPlane(context, id + "F19", {"entities" : qUnion([Q0]), "cplaneType" : CPlaneType.OFFSET, "offset" : 300 * mm, "width" : 150 * mm, "height" : 150 * mm});
        }
        {
            var Q0;
            Q0=makeQuery(id+"F1.opExtrude","SWEPT_BODY",BODY,{"disambiguationData":[OSD([sQuery(id+"F0.wireOp",EDGE,"E0"),sQuery(id+"F0.wireOp",EDGE,"E1"),sQuery(id+"F0.wireOp",EDGE,"E2"),sQuery(id+"F0.wireOp",EDGE,"E3"),sQuery(id+"F0.wireOp",EDGE,"E5"),sQuery(id+"F0.wireOp",EDGE,"E6")])]});
            var Q1;
            Q1=makeQuery(id+"F18.opPattern","COPY",BODY,{"derivedFrom":makeQuery(id+"F15.opExtrude","SWEPT_BODY",BODY,{"disambiguationData":[OSD([sQuery(id+"F14.wireOp",EDGE,"E117"),sQuery(id+"F14.wireOp",EDGE,"E118"),sQuery(id+"F14.wireOp",EDGE,"E119"),sQuery(id+"F14.wireOp",EDGE,"E120"),sQuery(id+"F14.wireOp",EDGE,"E126"),sQuery(id+"F14.wireOp",EDGE,"E127"),sQuery(id+"F14.wireOp",EDGE,"E128")])]}),"instanceName":"1"});
            var Q2;
            Q2=makeQuery(id+"F8.opExtrude","SWEPT_BODY",BODY,{"disambiguationData":[OSD([sQuery(id+"F7.wireOp",EDGE,"E57"),sQuery(id+"F7.wireOp",EDGE,"E58"),sQuery(id+"F7.wireOp",EDGE,"E59"),sQuery(id+"F7.wireOp",EDGE,"E60"),sQuery(id+"F7.wireOp",EDGE,"E62"),sQuery(id+"F7.wireOp",EDGE,"E65"),sQuery(id+"F7.wireOp",EDGE,"E66"),sQuery(id+"F7.wireOp",EDGE,"a3dc1NE5-J77q-sxHU-Vcka-XX6ci5muAKLQ")])]});
            var Q3;
            Q3=makeQuery(id+"F13.opPattern","COPY",BODY,{"derivedFrom":makeQuery(id+"F1.opExtrude","SWEPT_BODY",BODY,{"disambiguationData":[OSD([sQuery(id+"F0.wireOp",EDGE,"E0"),sQuery(id+"F0.wireOp",EDGE,"E1"),sQuery(id+"F0.wireOp",EDGE,"E2"),sQuery(id+"F0.wireOp",EDGE,"E3"),sQuery(id+"F0.wireOp",EDGE,"E5"),sQuery(id+"F0.wireOp",EDGE,"E6")])]}),"instanceName":"1"});
            var Q4;
            Q4=makeQuery(id+"F15.opExtrude","SWEPT_BODY",BODY,{"disambiguationData":[OSD([sQuery(id+"F14.wireOp",EDGE,"E113"),sQuery(id+"F14.wireOp",EDGE,"E114"),sQuery(id+"F14.wireOp",EDGE,"E115"),sQuery(id+"F14.wireOp",EDGE,"E116"),sQuery(id+"F14.wireOp",EDGE,"E125"),sQuery(id+"F14.wireOp",EDGE,"E129"),sQuery(id+"F14.wireOp",EDGE,"E130")])]});
            var Q5;
            Q5=makeQuery(id+"F15.opExtrude","SWEPT_BODY",BODY,{"disambiguationData":[OSD([sQuery(id+"F14.wireOp",EDGE,"E117"),sQuery(id+"F14.wireOp",EDGE,"E118"),sQuery(id+"F14.wireOp",EDGE,"E119"),sQuery(id+"F14.wireOp",EDGE,"E120"),sQuery(id+"F14.wireOp",EDGE,"E126"),sQuery(id+"F14.wireOp",EDGE,"E127"),sQuery(id+"F14.wireOp",EDGE,"E128")])]});
            var Q6;
            Q6=makeQuery(id+"F18.opPattern","COPY",BODY,{"derivedFrom":makeQuery(id+"F15.opExtrude","SWEPT_BODY",BODY,{"disambiguationData":[OSD([sQuery(id+"F14.wireOp",EDGE,"E113"),sQuery(id+"F14.wireOp",EDGE,"E114"),sQuery(id+"F14.wireOp",EDGE,"E115"),sQuery(id+"F14.wireOp",EDGE,"E116"),sQuery(id+"F14.wireOp",EDGE,"E125"),sQuery(id+"F14.wireOp",EDGE,"E129"),sQuery(id+"F14.wireOp",EDGE,"E130")])]}),"instanceName":"1"});
            var Q7;
            Q7=makeQuery(id+"FXQwG3oA6umNqDY_4.opExtrude","SWEPT_BODY",BODY,{"disambiguationData":[OSD([sQuery(id+"FCqva40XrJ4V126_4.wireOp",EDGE,"78n3ciA1-uomn-yBy7-r25V-WP5mjnDSE51b"),sQuery(id+"FCqva40XrJ4V126_4.wireOp",EDGE,"Y7wIcyIb-FoVn-5xuj-phSf-5b2q6NPwGIWa"),sQuery(id+"FCqva40XrJ4V126_4.wireOp",EDGE,"lD3lK019-n7aM-jMCI-HHF9-xqF3XS0OYAXL"),sQuery(id+"FCqva40XrJ4V126_4.wireOp",EDGE,"R12ONif3-EaFE-nE2H-PnFe-9cwd8XNfsR2q"),sQuery(id+"FCqva40XrJ4V126_4.wireOp",EDGE,"ELFCeRas-l5d1-hcGD-FCQb-yX8VnA3mtWFh"),sQuery(id+"FCqva40XrJ4V126_4.wireOp",EDGE,"DLMsOrrG-DfZs-aLlZ-V3jN-I2WMqElGk50g"),sQuery(id+"FCqva40XrJ4V126_4.wireOp",EDGE,"UV9GXJqr-dj6A-OMwq-xkIZ-CN148UZTotel")])]});
            var Q8;
            Q8=qCreatedBy(id+"F19.planeOp",FACE);
            mirror(context, id + "F20", {"entities" : qUnion([Q0, Q1, Q2, Q3, Q4, Q5, Q6, Q7]), "mirrorPlane" : qUnion([Q8])});
        }
        {
            var Q0;
            Q0=qCreatedBy(id+"F19.planeOp",FACE);
            var sketch = newSketch(context, id + "F21", { "sketchPlane" : qUnion([Q0])});
            skCircle(sketch, "E131", {"center": v(-392.9, 1025) * mm, "radius": 5.9 * mm});
            skSolve(sketch);
        }
        {
            var Q0;
            Q0=qSketchRegion(id+"F21",true);
            extrude(context, id + "F22", {"entities" : qUnion([Q0]), "endBound" : BoundingType.SYMMETRIC, "depth" : 760 * mm, "offsetDistance" : 25 * mm});
        }
        {
            var Q0;
            Q0=qCreatedBy(id+"F19.planeOp",FACE);
            var sketch = newSketch(context, id + "F23", { "sketchPlane" : qUnion([Q0])});
            skCircle(sketch, "E132", {"center": v(-392.9, 1025) * mm, "radius": 30 * mm});
            skCircle(sketch, "E133", {"center": v(-392.9, 1025) * mm, "radius": 6.25 * mm});
            skSolve(sketch);
        }
        {
            var Q0;
            Q0=qSketchRegion(id+"F23",true);
            extrude(context, id + "F24", {"entities" : qUnion([Q0]), "endBound" : BoundingType.SYMMETRIC, "depth" : 590 * mm, "offsetDistance" : 25 * mm});
        }
        {
            var Q0;
            Q0=makeQuery(id+"F22.opExtrude","CAP_EDGE",EDGE,{"disambiguationData":[OSD([sQuery(id+"F21.wireOp",EDGE,"E131")])],"isStart":true});
            var Q1;
            Q1=makeQuery(id+"F22.opExtrude","CAP_EDGE",EDGE,{"disambiguationData":[OSD([sQuery(id+"F21.wireOp",EDGE,"E131")])],"isStart":false});
            chamfer(context, id + "F25", {"entities" : qUnion([Q0, Q1]), "width" : 2 * mm, "tangentPropagation" : true});
        }
        {
            var Q0;
            Q0=makeQuery(id+"F24.opExtrude","CAP_EDGE",EDGE,{"disambiguationData":[OSD([sQuery(id+"F23.wireOp",EDGE,"E132")])],"isStart":false});
            var Q1;
            Q1=makeQuery(id+"F24.opExtrude","CAP_EDGE",EDGE,{"disambiguationData":[OSD([sQuery(id+"F23.wireOp",EDGE,"E132")])],"isStart":true});
            chamfer(context, id + "F26", {"entities" : qUnion([Q0, Q1]), "width" : 5 * mm, "tangentPropagation" : true});
        }
        {
            var Q0;
            Q0=makeQuery(id+"F24.opExtrude","SWEPT_FACE",FACE,{"disambiguationData":[OSD([sQuery(id+"F23.wireOp",EDGE,"E132")])]});
            cPlane(context, id + "F27", {"entities" : qUnion([Q0]), "cplaneType" : CPlaneType.LINE_ANGLE, "offset" : 25 * mm, "angle" : 0 * degree, "width" : 150 * mm, "height" : 150 * mm});
        }
        {
            var Q0;
            {var subQ0=sQuery(id+"F0.wireOp",EDGE,"E0");Q0=makeQuery(id+"F4.boolean.opBoolean","SPLIT",FACE,{"disambiguationData":[TD([makeQuery(id+"F4.opExtrude","SWEPT_FACE",FACE,{"disambiguationData":[OSD([sQuery(id+"F3.wireOp",EDGE,"E20.MirrorCS")])]})])],"derivedFrom":makeQuery(id+"F1.opExtrude","SWEPT_FACE",FACE,{"disambiguationData":[OSD([subQ0])]})});}
            var sketch = newSketch(context, id + "F28", { "sketchPlane" : qUnion([Q0])});
            skLineSegment(sketch, "E134", {"start": v(0, 220) * mm, "end": v(0, 180) * mm});
            skLineSegment(sketch, "E135", {"start": v(-720, 180) * mm, "end": v(0, 180) * mm});
            skLineSegment(sketch, "E136", {"start": v(-720, 180) * mm, "end": v(-720, 220) * mm});
            skLineSegment(sketch, "E137", {"start": v(0, 220) * mm, "end": v(-720, 220) * mm});
            skLineSegment(sketch, "E138", {"start": v(-720, 200) * mm, "end": v(0, 200) * mm, "construction": true});
            skCircle(sketch, "E139", {"center": v(-30, 200) * mm, "radius": 6.25 * mm});
            skCircle(sketch, "E140", {"center": v(-690, 200) * mm, "radius": 6.25 * mm});
            skLineSegment(sketch, "E141", {"start": v(-720, 645) * mm, "end": v(-720, 605) * mm});
            skLineSegment(sketch, "E142", {"start": v(-720, 605) * mm, "end": v(0, 605) * mm});
            skLineSegment(sketch, "E143", {"start": v(0, 605) * mm, "end": v(0, 645) * mm});
            skLineSegment(sketch, "E144", {"start": v(0, 645) * mm, "end": v(-720, 645) * mm});
            skLineSegment(sketch, "E145", {"start": v(-720, 625) * mm, "end": v(0, 625) * mm, "construction": true});
            skCircle(sketch, "E146", {"center": v(-690, 625) * mm, "radius": 6.25 * mm});
            skCircle(sketch, "E147", {"center": v(-30, 625) * mm, "radius": 6.25 * mm});
            skSolve(sketch);
        }
        {
            var Q0;
            Q0=qSketchRegion(id+"F28",true);
            extrude(context, id + "F29", {"entities" : qUnion([Q0]), "depth" : 4 * mm, "offsetDistance" : 25 * mm});
        }
        {
            var Q0;
            Q0=makeQuery(id+"F29.opExtrude","SWEPT_EDGE",EDGE,{"disambiguationData":[OSD([sQuery(id+"F28.wireOp",EDGE,"E134"),sQuery(id+"F28.wireOp",EDGE,"E137")])]});
            var Q1;
            Q1=makeQuery(id+"F29.opExtrude","SWEPT_EDGE",EDGE,{"disambiguationData":[OSD([sQuery(id+"F28.wireOp",EDGE,"E134"),sQuery(id+"F28.wireOp",EDGE,"E135")])]});
            var Q2;
            Q2=makeQuery(id+"F29.opExtrude","SWEPT_EDGE",EDGE,{"disambiguationData":[OSD([sQuery(id+"F28.wireOp",EDGE,"E136"),sQuery(id+"F28.wireOp",EDGE,"E137")])]});
            var Q3;
            Q3=makeQuery(id+"F29.opExtrude","SWEPT_EDGE",EDGE,{"disambiguationData":[OSD([sQuery(id+"F28.wireOp",EDGE,"E135"),sQuery(id+"F28.wireOp",EDGE,"E136")])]});
            var Q4;
            Q4=makeQuery(id+"F29.opExtrude","SWEPT_EDGE",EDGE,{"disambiguationData":[OSD([sQuery(id+"F28.wireOp",EDGE,"E141"),sQuery(id+"F28.wireOp",EDGE,"E144")])]});
            var Q5;
            Q5=makeQuery(id+"F29.opExtrude","SWEPT_EDGE",EDGE,{"disambiguationData":[OSD([sQuery(id+"F28.wireOp",EDGE,"E141"),sQuery(id+"F28.wireOp",EDGE,"E142")])]});
            var Q6;
            Q6=makeQuery(id+"F29.opExtrude","SWEPT_EDGE",EDGE,{"disambiguationData":[OSD([sQuery(id+"F28.wireOp",EDGE,"E143"),sQuery(id+"F28.wireOp",EDGE,"E144")])]});
            var Q7;
            Q7=makeQuery(id+"F29.opExtrude","SWEPT_EDGE",EDGE,{"disambiguationData":[OSD([sQuery(id+"F28.wireOp",EDGE,"E142"),sQuery(id+"F28.wireOp",EDGE,"E143")])]});
            fillet(context, id + "F30", {"entities" : qUnion([Q0, Q1, Q2, Q3, Q4, Q5, Q6, Q7]), "radius" : 7.5 * mm, "tangentPropagation" : true, "allowEdgeOverflow" : false});
        }
        {
            var Q0;
            Q0=makeQuery(id+"F29.opExtrude","SWEPT_BODY",BODY,{"disambiguationData":[OSD([sQuery(id+"F28.wireOp",EDGE,"E134"),sQuery(id+"F28.wireOp",EDGE,"E135"),sQuery(id+"F28.wireOp",EDGE,"E136"),sQuery(id+"F28.wireOp",EDGE,"E137"),sQuery(id+"F28.wireOp",EDGE,"E139"),sQuery(id+"F28.wireOp",EDGE,"E140")])]});
            var Q1;
            Q1=makeQuery(id+"F29.opExtrude","SWEPT_BODY",BODY,{"disambiguationData":[OSD([sQuery(id+"F28.wireOp",EDGE,"E141"),sQuery(id+"F28.wireOp",EDGE,"E142"),sQuery(id+"F28.wireOp",EDGE,"E143"),sQuery(id+"F28.wireOp",EDGE,"E144"),sQuery(id+"F28.wireOp",EDGE,"E146"),sQuery(id+"F28.wireOp",EDGE,"E147")])]});
            var Q2;
            Q2=qCreatedBy(id+"F12.planeOp",FACE);
            mirror(context, id + "F31", {"entities" : qUnion([Q0, Q1]), "mirrorPlane" : qUnion([Q2])});
        }
    });
